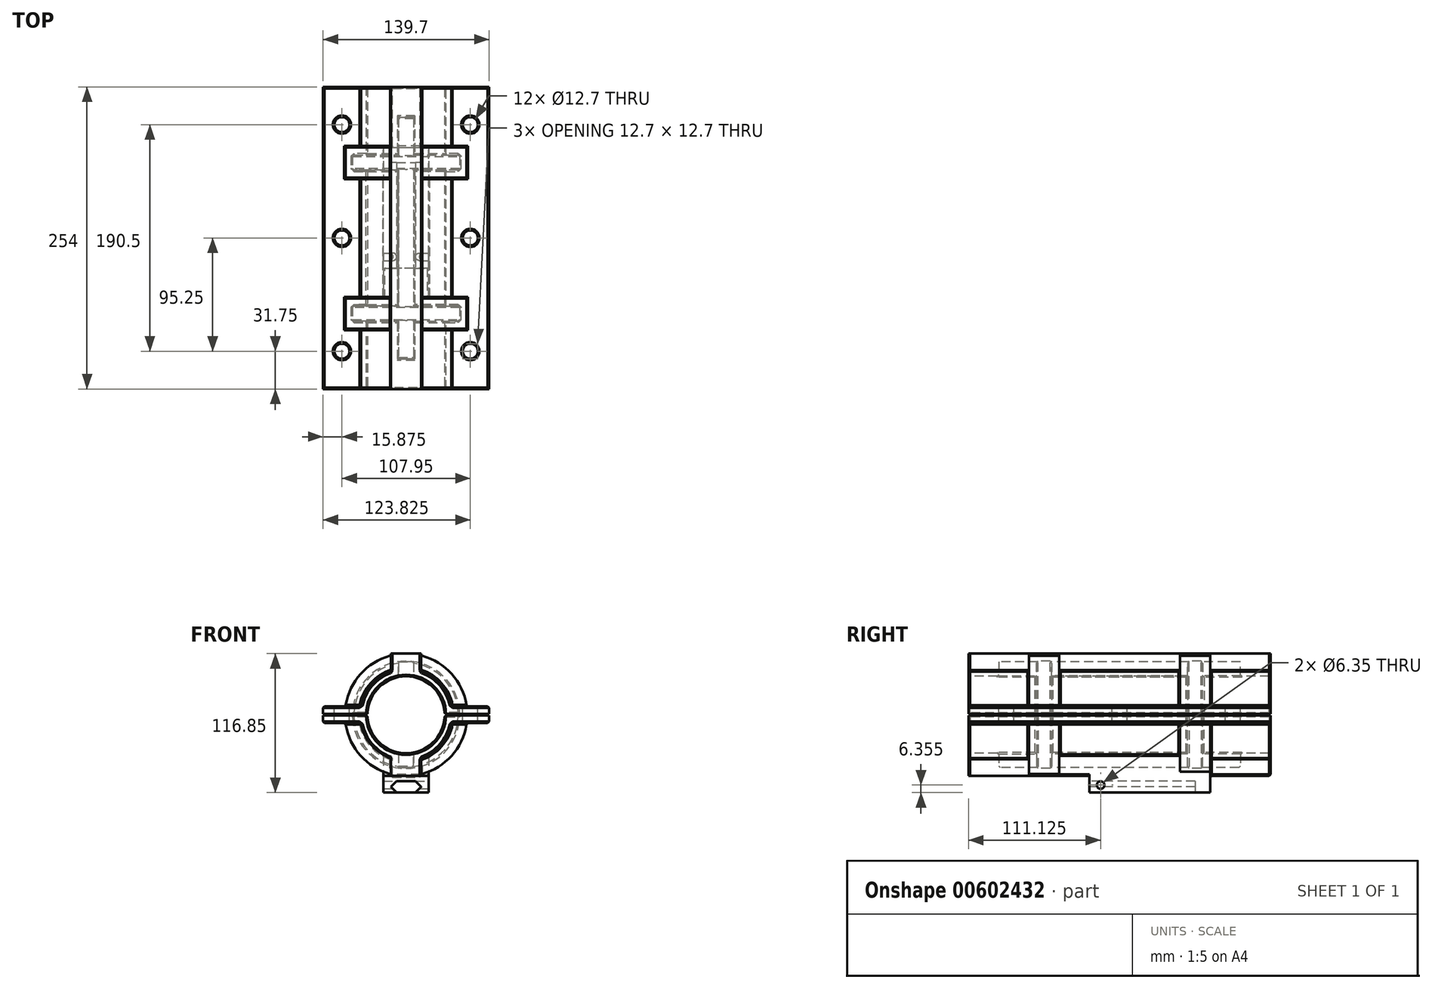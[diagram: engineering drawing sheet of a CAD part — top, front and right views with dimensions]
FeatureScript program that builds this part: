
annotation { "Feature Type Name" : "Feature", "Feature Type Description" : "" }
export const myFeature = defineFeature(function(context is Context, id is Id, definition is map)
    precondition{}
    {
        {
            var Q0;
            Q0=qCreatedBy(makeId("Front.planeOp"),FACE);
            var sketch = newSketch(context, id + "F0", { "sketchPlane" : qUnion([Q0])});
            skArc(sketch, "E0", {"start": v(-32.38, -0.64) * mm, "mid": v(0, -32.39) * mm, "end": v(32.38, -0.63) * mm});
            skLineSegment(sketch, "E1", {"start": v(0, 38.74) * mm, "end": v(0, -51.44) * mm, "construction": true});
            skLineSegment(sketch, "E2", {"start": v(-32.39, 0) * mm, "end": v(32.39, 0) * mm, "construction": true});
            skLineSegment(sketch, "E3", {"start": v(-32.38, 0.63) * mm, "end": v(-69.85, 0.63) * mm});
            skLineSegment(sketch, "E4", {"start": v(-69.85, 0.64) * mm, "end": v(-69.85, 6.98) * mm});
            skLineSegment(sketch, "E5", {"start": v(-69.85, 6.98) * mm, "end": v(-38.1, 6.98) * mm});
            skLineSegment(sketch, "E6.MirrorCS", {"start": v(32.38, 0.63) * mm, "end": v(69.85, 0.63) * mm});
            skLineSegment(sketch, "E7.MirrorCS", {"start": v(69.85, 0.64) * mm, "end": v(69.85, 6.98) * mm});
            skLineSegment(sketch, "E8.MirrorCS", {"start": v(69.85, 6.98) * mm, "end": v(38.1, 6.98) * mm});
            skLineSegment(sketch, "E9.MirrorCS", {"start": v(-32.38, -0.63) * mm, "end": v(-69.85, -0.63) * mm});
            skLineSegment(sketch, "E10.MirrorCS", {"start": v(-69.85, -6.98) * mm, "end": v(-38.1, -6.98) * mm});
            skLineSegment(sketch, "E11.MirrorCS", {"start": v(-69.85, -0.64) * mm, "end": v(-69.85, -6.98) * mm});
            skLineSegment(sketch, "E12.MirrorCS", {"start": v(69.85, -6.98) * mm, "end": v(38.1, -6.98) * mm});
            skLineSegment(sketch, "E13.MirrorCS", {"start": v(69.85, -0.64) * mm, "end": v(69.85, -6.98) * mm});
            skLineSegment(sketch, "E14.MirrorCS", {"start": v(32.38, -0.63) * mm, "end": v(69.85, -0.63) * mm});
            skArc(sketch, "E15.trimOffspring", {"start": v(-38.1, -6.98) * mm, "mid": v(-29.4, -25.22) * mm, "end": v(-12.7, -36.6) * mm});
            skArc(sketch, "E16.trimOffspring", {"start": v(38.1, 6.98) * mm, "mid": v(29.4, 25.22) * mm, "end": v(12.7, 36.6) * mm});
            skArc(sketch, "E17.trimOffspring", {"start": v(32.38, 0.63) * mm, "mid": v(0, 32.39) * mm, "end": v(-32.38, 0.64) * mm});
            skLineSegment(sketch, "E18", {"start": v(-12.7, 36.6) * mm, "end": v(-12.7, 51.44) * mm});
            skLineSegment(sketch, "E19", {"start": v(12.7, 51.44) * mm, "end": v(12.7, 36.6) * mm});
            skArc(sketch, "E20.trimOffspring", {"start": v(-12.7, 36.6) * mm, "mid": v(-29.4, 25.22) * mm, "end": v(-38.1, 6.98) * mm});
            skLineSegment(sketch, "E21", {"start": v(-12.7, 51.44) * mm, "end": v(12.7, 51.44) * mm});
            skLineSegment(sketch, "E22", {"start": v(-12.7, -36.6) * mm, "end": v(-12.7, -51.44) * mm});
            skLineSegment(sketch, "E23", {"start": v(-12.7, -51.44) * mm, "end": v(12.7, -51.44) * mm});
            skLineSegment(sketch, "E24", {"start": v(12.7, -51.44) * mm, "end": v(12.7, -36.6) * mm});
            skLineSegment(sketch, "E25", {"start": v(0, 38.74) * mm, "end": v(0, 51.44) * mm, "construction": true});
            skArc(sketch, "E26.trimOffspring", {"start": v(12.7, -36.6) * mm, "mid": v(29.4, -25.22) * mm, "end": v(38.1, -6.98) * mm});
            skCircle(sketch, "E27", {"center": v(0, 0) * mm, "radius": 38.74 * mm, "construction": true});
            skPoint(sketch, "E28", {"position": v(0, -38.74) * mm});
            skSolve(sketch);
        }
        {
            var Q0;
            Q0 = qSketchRegion(id + "F0", true);
            extrude(context, id + "F1", {"entities" : qUnion([Q0]), "oppositeDirection" : true, "depth" : 254 * mm, "offsetDistance" : 25.4 * mm});
        }
        {
            var Q0;
            Q0=qCreatedBy(makeId("Top.planeOp"),FACE);
            var sketch = newSketch(context, id + "F2", { "sketchPlane" : qUnion([Q0])});
            skLineSegment(sketch, "E29", {"start": v(0, 0) * mm, "end": v(0, 254) * mm, "construction": true});
            skLineSegment(sketch, "E30", {"start": v(0, 254) * mm, "end": v(32.39, 254) * mm, "construction": true});
            skLineSegment(sketch, "E31", {"start": v(32.38, 254) * mm, "end": v(32.39, 196.85) * mm});
            skLineSegment(sketch, "E32", {"start": v(32.39, 69.85) * mm, "end": v(45.09, 69.85) * mm});
            skLineSegment(sketch, "E33", {"start": v(45.09, 69.85) * mm, "end": v(45.09, 57.15) * mm});
            skLineSegment(sketch, "E34", {"start": v(45.09, 57.15) * mm, "end": v(32.39, 57.15) * mm});
            skLineSegment(sketch, "E35", {"start": v(32.39, 57.15) * mm, "end": v(32.39, 0) * mm});
            skLineSegment(sketch, "E36", {"start": v(32.39, 0) * mm, "end": v(38.74, 0) * mm});
            skLineSegment(sketch, "E37", {"start": v(38.74, 0) * mm, "end": v(38.74, 50.8) * mm});
            skLineSegment(sketch, "E38", {"start": v(38.74, 50.8) * mm, "end": v(51.44, 50.8) * mm});
            skLineSegment(sketch, "E39", {"start": v(51.44, 50.8) * mm, "end": v(51.44, 76.2) * mm});
            skLineSegment(sketch, "E40", {"start": v(51.44, 76.2) * mm, "end": v(38.74, 76.2) * mm});
            skLineSegment(sketch, "E41", {"start": v(38.74, 76.2) * mm, "end": v(38.74, 177.8) * mm});
            skLineSegment(sketch, "E42", {"start": v(38.74, 254) * mm, "end": v(32.39, 254) * mm});
            skLineSegment(sketch, "E43", {"start": v(69.85, 127) * mm, "end": v(-69.85, 127) * mm, "construction": true});
            skPoint(sketch, "E43.startSnap0", {"position": v(0, 127) * mm});
            skLineSegment(sketch, "E44.MirrorCS", {"start": v(51.44, 177.8) * mm, "end": v(38.74, 177.8) * mm});
            skLineSegment(sketch, "E45.MirrorCS", {"start": v(51.44, 203.2) * mm, "end": v(51.44, 177.8) * mm});
            skLineSegment(sketch, "E46.MirrorCS", {"start": v(38.74, 203.2) * mm, "end": v(51.44, 203.2) * mm});
            skLineSegment(sketch, "E47.MirrorCS", {"start": v(45.09, 196.85) * mm, "end": v(32.38, 196.85) * mm});
            skLineSegment(sketch, "E48.MirrorCS", {"start": v(32.39, 184.15) * mm, "end": v(45.09, 184.15) * mm});
            skLineSegment(sketch, "E49.MirrorCS", {"start": v(45.09, 184.15) * mm, "end": v(45.09, 196.85) * mm});
            skLineSegment(sketch, "E50.trimOffspring", {"start": v(38.73, 203.2) * mm, "end": v(38.73, 254) * mm});
            skLineSegment(sketch, "E51.trimOffspring", {"start": v(32.39, 184.15) * mm, "end": v(32.39, 69.85) * mm});
            skSolve(sketch);
        }
        {
            var Q0;
            Q0 = qSketchRegion(id + "F2", true);
            var Q1;
            Q1=sQuery(id+"F2.wireOp",EDGE,"E29");
            revolve(context, id + "F3", {"operationType" : NewBodyOperationType.ADD, "entities" : qUnion([Q0]), "axis" : qUnion([Q1]), "revolveType" : RevolveType.FULL});
        }
        {
            var Q0;
            Q0=qCreatedBy(makeId("Top.planeOp"),FACE);
            var sketch = newSketch(context, id + "F4", { "sketchPlane" : qUnion([Q0])});
            skLineSegment(sketch, "E52", {"start": v(0, 0) * mm, "end": v(0, 254) * mm, "construction": true});
            skLineSegment(sketch, "E53", {"start": v(0, 254) * mm, "end": v(32.39, 254) * mm, "construction": true});
            skLineSegment(sketch, "E54", {"start": v(32.39, 254) * mm, "end": v(32.39, 196.85) * mm, "construction": true});
            skLineSegment(sketch, "E55", {"start": v(32.39, 196.85) * mm, "end": v(45.08, 196.85) * mm});
            skLineSegment(sketch, "E56", {"start": v(45.08, 196.85) * mm, "end": v(45.08, 184.15) * mm});
            skLineSegment(sketch, "E57", {"start": v(45.08, 184.15) * mm, "end": v(32.39, 184.15) * mm});
            skLineSegment(sketch, "E58", {"start": v(32.39, 184.15) * mm, "end": v(32.39, 196.85) * mm});
            skLineSegment(sketch, "E59", {"start": v(0, 127) * mm, "end": v(69.85, 127) * mm, "construction": true});
            skPoint(sketch, "E59.endSnap0", {"position": v(0, 127) * mm});
            skLineSegment(sketch, "E60.MirrorCS", {"start": v(32.39, 69.85) * mm, "end": v(32.39, 57.15) * mm});
            skLineSegment(sketch, "E61.MirrorCS", {"start": v(32.39, 57.15) * mm, "end": v(45.09, 57.15) * mm});
            skLineSegment(sketch, "E62.MirrorCS", {"start": v(45.09, 57.15) * mm, "end": v(45.09, 69.85) * mm});
            skLineSegment(sketch, "E63.MirrorCS", {"start": v(45.09, 69.85) * mm, "end": v(32.39, 69.85) * mm});
            skSolve(sketch);
        }
        {
            var Q0;
            Q0 = qSketchRegion(id + "F4", true);
            var Q1;
            Q1=sQuery(id+"F4.wireOp",EDGE,"E52");
            revolve(context, id + "F5", {"operationType" : NewBodyOperationType.REMOVE, "entities" : qUnion([Q0]), "axis" : qUnion([Q1]), "revolveType" : RevolveType.FULL, "oppositeDirection" : true});
        }
        {
            var Q0;
            Q0=qCreatedBy(makeId("Front.planeOp"),FACE);
            var sketch = newSketch(context, id + "F6", { "sketchPlane" : qUnion([Q0])});
            skLineSegment(sketch, "E64", {"start": v(0, -32.39) * mm, "end": v(0, 32.39) * mm, "construction": true});
            skLineSegment(sketch, "E65", {"start": v(-69.85, 0) * mm, "end": v(69.85, 0) * mm, "construction": true});
            skLineSegment(sketch, "E66", {"start": v(-69.85, 0) * mm, "end": v(-69.85, 0.64) * mm});
            skLineSegment(sketch, "E67", {"start": v(-69.85, 0.64) * mm, "end": v(69.85, 0.64) * mm});
            skLineSegment(sketch, "E68", {"start": v(69.85, 0.64) * mm, "end": v(69.85, 0) * mm});
            skLineSegment(sketch, "E69.MirrorCS", {"start": v(-69.85, 0) * mm, "end": v(-69.85, -0.64) * mm});
            skLineSegment(sketch, "E70.MirrorCS", {"start": v(-69.85, -0.64) * mm, "end": v(69.85, -0.64) * mm});
            skLineSegment(sketch, "E71.MirrorCS", {"start": v(69.85, -0.64) * mm, "end": v(69.85, 0) * mm});
            skSolve(sketch);
        }
        {
            var Q0;
            Q0 = qSketchRegion(id + "F6", true);
            extrude(context, id + "F7", {"entities" : qUnion([Q0]), "operationType" : NewBodyOperationType.REMOVE, "oppositeDirection" : true, "depth" : 254 * mm, "offsetDistance" : 25.4 * mm});
        }
        {
            var Q0;
            Q0=makeQuery(id+"F1.opExtrude","SWEPT_FACE",FACE,{"disambiguationData":[OSD([sQuery(id+"F0.wireOp",EDGE,"E23")])]});
            cPlane(context, id + "F8", {"entities" : qUnion([Q0]), "cplaneType" : CPlaneType.OFFSET, "offset" : 13.97 * mm, "width" : 152.4 * mm, "height" : 152.4 * mm});
        }
        {
            var Q0;
            Q0=qCreatedBy(id+"F8.planeOp",FACE);
            var sketch = newSketch(context, id + "F9", { "sketchPlane" : qUnion([Q0])});
            skLineSegment(sketch, "E72", {"start": v(0, 0) * mm, "end": v(0, -254) * mm, "construction": true});
            skLineSegment(sketch, "E73.bottom", {"start": v(-19.05, -101.6) * mm, "end": v(19.05, -101.6) * mm});
            skLineSegment(sketch, "E73.top", {"start": v(-19.05, -203.2) * mm, "end": v(19.05, -203.2) * mm});
            skLineSegment(sketch, "E73.left", {"start": v(-19.05, -101.6) * mm, "end": v(-19.05, -203.2) * mm});
            skLineSegment(sketch, "E73.right", {"start": v(19.05, -101.6) * mm, "end": v(19.05, -203.2) * mm});
            skPoint(sketch, "E73.middle", {"position": v(0, -152.4) * mm});
            skSolve(sketch);
        }
        {
            var Q0;
            Q0 = qSketchRegion(id + "F9", true);
            extrude(context, id + "F10", {"entities" : qUnion([Q0]), "operationType" : NewBodyOperationType.ADD, "endBound" : BoundingType.UP_TO_NEXT, "oppositeDirection" : true, "depth" : 25.4 * mm, "offsetDistance" : 25.4 * mm});
        }
        {
            var Q0;
            Q0=makeQuery(id+"F10.opExtrude","SWEPT_FACE",FACE,{"disambiguationData":[OSD([sQuery(id+"F9.wireOp",EDGE,"E73.bottom")])]});
            var sketch = newSketch(context, id + "F11", { "sketchPlane" : qUnion([Q0])});
            skLineSegment(sketch, "E74", {"start": v(0, -65.4) * mm, "end": v(-7.94, -65.4) * mm});
            skLineSegment(sketch, "E75", {"start": v(-12.7, -60.64) * mm, "end": v(-7.94, -65.4) * mm});
            skLineSegment(sketch, "E76", {"start": v(-7.94, -55.88) * mm, "end": v(-12.7, -60.64) * mm});
            skLineSegment(sketch, "E77", {"start": v(-7.94, -55.88) * mm, "end": v(0, -55.88) * mm});
            skLineSegment(sketch, "E78", {"start": v(0, -51.44) * mm, "end": v(0, -65.4) * mm, "construction": true});
            skLineSegment(sketch, "E79.MirrorCS", {"start": v(0, -65.4) * mm, "end": v(7.94, -65.4) * mm});
            skLineSegment(sketch, "E80.MirrorCS", {"start": v(12.7, -60.64) * mm, "end": v(7.94, -65.4) * mm});
            skLineSegment(sketch, "E81.MirrorCS", {"start": v(7.94, -55.88) * mm, "end": v(12.7, -60.64) * mm});
            skLineSegment(sketch, "E82.MirrorCS", {"start": v(7.94, -55.88) * mm, "end": v(0, -55.88) * mm});
            skSolve(sketch);
        }
        {
            var Q0;
            Q0 = qSketchRegion(id + "F11", true);
            extrude(context, id + "F12", {"entities" : qUnion([Q0]), "operationType" : NewBodyOperationType.REMOVE, "oppositeDirection" : true, "depth" : 88.9 * mm, "offsetDistance" : 25.4 * mm});
        }
        {
            var Q0;
            {var subQ2=sQuery(id+"F9.wireOp",EDGE,"E73.right");Q0=makeQuery(id+"F10.boolean.opBoolean","SPLIT",FACE,{"disambiguationData":[TD([makeQuery(id+"F1.opExtrude","SWEPT_FACE",FACE,{"disambiguationData":[OSD([sQuery(id+"F0.wireOp",EDGE,"E26.trimOffspring")])]})])],"derivedFrom":makeQuery(id+"F10.opExtrude","SWEPT_FACE",FACE,{"disambiguationData":[OSD([subQ2])]})});}
            var sketch = newSketch(context, id + "F13", { "sketchPlane" : qUnion([Q0])});
            skCircle(sketch, "E83", {"center": v(111.12, -59.06) * mm, "radius": 3.18 * mm});
            skSolve(sketch);
        }
        {
            var Q0;
            Q0 = qSketchRegion(id + "F13", true);
            extrude(context, id + "F14", {"entities" : qUnion([Q0]), "operationType" : NewBodyOperationType.REMOVE, "endBound" : BoundingType.THROUGH_ALL, "oppositeDirection" : true, "depth" : 25.4 * mm, "offsetDistance" : 25.4 * mm});
        }
        {
            var Q0;
            {var subQ0=sQuery(id+"F0.wireOp",EDGE,"E17.trimOffspring");var subQ1=sQuery(id+"F0.wireOp",EDGE,"E15.trimOffspring");var subQ2=sQuery(id+"F0.wireOp",EDGE,"E14.MirrorCS");var subQ3=sQuery(id+"F0.wireOp",EDGE,"E13.MirrorCS");var subQ4=sQuery(id+"F0.wireOp",EDGE,"E12.MirrorCS");var subQ5=sQuery(id+"F0.wireOp",EDGE,"E0");var subQ6=sQuery(id+"F0.wireOp",EDGE,"E9.MirrorCS");var subQ7=sQuery(id+"F0.wireOp",EDGE,"E10.MirrorCS");var subQ8=sQuery(id+"F0.wireOp",EDGE,"E22");var subQ9=sQuery(id+"F0.wireOp",EDGE,"E11.MirrorCS");var subQ10=sQuery(id+"F0.wireOp",EDGE,"E23");var subQ11=sQuery(id+"F0.wireOp",EDGE,"E24");var subQ12=sQuery(id+"F0.wireOp",EDGE,"E26.trimOffspring");Q0=makeQuery(id+"F7.boolean.opBoolean","SPLIT",FACE,{"disambiguationData":[TD([makeQuery(id+"F1.opExtrude","SWEPT_FACE",FACE,{"disambiguationData":[OSD([subQ6])]})])],"derivedFrom":makeQuery(id+"F3.boolean.opBoolean","MERGE",FACE,{"derivedFrom":[makeQuery(id+"F1.opExtrude","CAP_FACE",FACE,{"disambiguationData":[OSD([subQ5,subQ6,subQ7,subQ9,subQ4,subQ3,subQ2,subQ1,subQ8,subQ10,subQ11,subQ12])],"isStart":true}),makeQuery(id+"F1.opExtrude","CAP_FACE",FACE,{"disambiguationData":[OSD([sQuery(id+"F0.wireOp",EDGE,"E3"),sQuery(id+"F0.wireOp",EDGE,"E4"),sQuery(id+"F0.wireOp",EDGE,"E5"),sQuery(id+"F0.wireOp",EDGE,"E6.MirrorCS"),sQuery(id+"F0.wireOp",EDGE,"E7.MirrorCS"),sQuery(id+"F0.wireOp",EDGE,"E8.MirrorCS"),sQuery(id+"F0.wireOp",EDGE,"E16.trimOffspring"),subQ0,sQuery(id+"F0.wireOp",EDGE,"E18"),sQuery(id+"F0.wireOp",EDGE,"E19"),sQuery(id+"F0.wireOp",EDGE,"E20.trimOffspring"),sQuery(id+"F0.wireOp",EDGE,"E21")])],"isStart":true}),makeQuery(id+"F3.opRevolve","SWEPT_FACE",FACE,{"disambiguationData":[OSD([sQuery(id+"F2.wireOp",EDGE,"E36")])]})]})});}
            cPlane(context, id + "F15", {"entities" : qUnion([Q0]), "cplaneType" : CPlaneType.OFFSET, "offset" : 25.4 * mm, "oppositeDirection" : true, "width" : 152.4 * mm, "height" : 152.4 * mm});
        }
        {
            var Q0;
            Q0=qCreatedBy(id+"F15.planeOp",FACE);
            var sketch = newSketch(context, id + "F16", { "sketchPlane" : qUnion([Q0])});
            skLineSegment(sketch, "E84", {"start": v(0, 51.44) * mm, "end": v(0, -51.44) * mm, "construction": true});
            skLineSegment(sketch, "E85", {"start": v(-6.35, 44.46) * mm, "end": v(6.35, 44.46) * mm});
            skLineSegment(sketch, "E86", {"start": v(6.35, 44.46) * mm, "end": v(6.35, 31.76) * mm});
            skLineSegment(sketch, "E87", {"start": v(6.35, 31.76) * mm, "end": v(-6.35, 31.76) * mm});
            skLineSegment(sketch, "E88", {"start": v(-6.35, 31.76) * mm, "end": v(-6.35, 44.46) * mm});
            skLineSegment(sketch, "E89", {"start": v(-62.32, 0) * mm, "end": v(62.17, 0) * mm, "construction": true});
            skLineSegment(sketch, "E90.MirrorCS", {"start": v(6.35, -31.76) * mm, "end": v(-6.35, -31.76) * mm});
            skLineSegment(sketch, "E91.MirrorCS", {"start": v(6.35, -44.46) * mm, "end": v(6.35, -31.76) * mm});
            skLineSegment(sketch, "E92.MirrorCS", {"start": v(-6.35, -44.46) * mm, "end": v(6.35, -44.46) * mm});
            skLineSegment(sketch, "E93.MirrorCS", {"start": v(-6.35, -31.76) * mm, "end": v(-6.35, -44.46) * mm});
            skSolve(sketch);
        }
        {
            var Q0;
            Q0 = qSketchRegion(id + "F16", true);
            extrude(context, id + "F17", {"entities" : qUnion([Q0]), "operationType" : NewBodyOperationType.REMOVE, "oppositeDirection" : true, "depth" : 203.2 * mm, "offsetDistance" : 25.4 * mm});
        }
        {
            var Q0;
            {var subQ2=sQuery(id+"F0.wireOp",EDGE,"E23");Q0=makeQuery(id+"F10.boolean.opBoolean","SPLIT",FACE,{"disambiguationData":[TD([makeQuery(id+"F3.opRevolve","SWEPT_FACE",FACE,{"disambiguationData":[OSD([sQuery(id+"F2.wireOp",EDGE,"E36")])]})])],"derivedFrom":makeQuery(id+"F1.opExtrude","SWEPT_FACE",FACE,{"disambiguationData":[OSD([subQ2])]})});}
            var sketch = newSketch(context, id + "F18", { "sketchPlane" : qUnion([Q0])});
            skLineSegment(sketch, "E94.bottom", {"start": v(-12.7, -101.6) * mm, "end": v(-19.05, -101.6) * mm});
            skLineSegment(sketch, "E94.top", {"start": v(-12.7, -76.2) * mm, "end": v(-19.05, -76.2) * mm});
            skLineSegment(sketch, "E94.left", {"start": v(-12.7, -101.6) * mm, "end": v(-12.7, -76.2) * mm});
            skLineSegment(sketch, "E94.right", {"start": v(-19.05, -101.6) * mm, "end": v(-19.05, -76.2) * mm});
            skLineSegment(sketch, "E95", {"start": v(0, 0) * mm, "end": v(0, -101.6) * mm, "construction": true});
            skLineSegment(sketch, "E96.MirrorCS", {"start": v(12.7, -101.6) * mm, "end": v(12.7, -76.2) * mm});
            skLineSegment(sketch, "E97.MirrorCS", {"start": v(12.7, -76.2) * mm, "end": v(19.05, -76.2) * mm});
            skLineSegment(sketch, "E98.MirrorCS", {"start": v(19.05, -101.6) * mm, "end": v(19.05, -76.2) * mm});
            skLineSegment(sketch, "E99.MirrorCS", {"start": v(12.7, -101.6) * mm, "end": v(19.05, -101.6) * mm});
            skSolve(sketch);
        }
        {
            var Q0;
            Q0 = qSketchRegion(id + "F18", true);
            extrude(context, id + "F19", {"entities" : qUnion([Q0]), "operationType" : NewBodyOperationType.ADD, "endBound" : BoundingType.UP_TO_NEXT, "oppositeDirection" : true, "depth" : 25.4 * mm, "offsetDistance" : 25.4 * mm});
        }
        {
            var Q0;
            {var subQ1=sQuery(id+"F0.wireOp",EDGE,"E4");var subQ22=sQuery(id+"F0.wireOp",EDGE,"E5");Q0=makeQuery(id+"F3.boolean.opBoolean","SPLIT",FACE,{"disambiguationData":[TD([makeQuery(id+"F1.opExtrude","SWEPT_FACE",FACE,{"disambiguationData":[OSD([subQ1])]})])],"derivedFrom":makeQuery(id+"F1.opExtrude","SWEPT_FACE",FACE,{"disambiguationData":[OSD([subQ22])]})});}
            var sketch = newSketch(context, id + "F20", { "sketchPlane" : qUnion([Q0])});
            skCircle(sketch, "E100", {"center": v(-53.98, 222.25) * mm, "radius": 6.35 * mm});
            skLineSegment(sketch, "E101", {"start": v(-53.98, 222.25) * mm, "end": v(-53.98, 127) * mm, "construction": true});
            skPoint(sketch, "E101.endSnap0", {"position": v(-69.85, 127) * mm});
            skCircle(sketch, "E102", {"center": v(-53.98, 127) * mm, "radius": 6.35 * mm});
            skLineSegment(sketch, "E103", {"start": v(-53.98, 127) * mm, "end": v(-69.85, 127) * mm, "construction": true});
            skCircle(sketch, "E104.MirrorC", {"center": v(-53.98, 31.75) * mm, "radius": 6.35 * mm});
            skLineSegment(sketch, "E105", {"start": v(0, 0) * mm, "end": v(0, 254) * mm, "construction": true});
            skCircle(sketch, "E106.MirrorC", {"center": v(53.97, 222.25) * mm, "radius": 6.35 * mm});
            skCircle(sketch, "E107.MirrorC", {"center": v(53.98, 127) * mm, "radius": 6.35 * mm});
            skCircle(sketch, "E108.MirrorC", {"center": v(53.98, 31.75) * mm, "radius": 6.35 * mm});
            skSolve(sketch);
        }
        {
            var Q0;
            Q0 = qSketchRegion(id + "F20", true);
            extrude(context, id + "F21", {"entities" : qUnion([Q0]), "operationType" : NewBodyOperationType.REMOVE, "endBound" : BoundingType.THROUGH_ALL, "oppositeDirection" : true, "depth" : 25.4 * mm, "offsetDistance" : 25.4 * mm});
        }
        {
            var Q0;
            Q0=makeQuery(id+"F3.boolean.opBoolean","INTERSECT",EDGE,{"derivedFrom":[makeQuery(id+"F1.opExtrude","SWEPT_FACE",FACE,{"disambiguationData":[OSD([sQuery(id+"F0.wireOp",EDGE,"E19")])]}),makeQuery(id+"F3.opRevolve","SWEPT_FACE",FACE,{"disambiguationData":[OSD([sQuery(id+"F2.wireOp",EDGE,"E45.MirrorCS")])]})]});
            var Q1;
            {var subQ0=sQuery(id+"F0.wireOp",EDGE,"E16.trimOffspring");var subQ1=sQuery(id+"F0.wireOp",EDGE,"E19");Q1=makeQuery(id+"F3.boolean.opBoolean","SPLIT",EDGE,{"disambiguationData":[TD([makeQuery(id+"F3.opRevolve","SWEPT_FACE",FACE,{"disambiguationData":[OSD([sQuery(id+"F2.wireOp",EDGE,"E36")])]})])],"derivedFrom":makeQuery(id+"F1.opExtrude","SWEPT_EDGE",EDGE,{"disambiguationData":[OSD([subQ0,subQ1])]})});}
            var Q2;
            {var subQ0=sQuery(id+"F2.wireOp",EDGE,"E38");Q2=makeQuery(id+"F3.boolean.opBoolean","SPLIT",EDGE,{"disambiguationData":[topologyDisambiguationEdgeConnected([makeQuery(id+"F1.opExtrude","SWEPT_FACE",FACE,{"disambiguationData":[OSD([sQuery(id+"F0.wireOp",EDGE,"E16.trimOffspring")])]}),makeQuery(id+"F3.opRevolve","SWEPT_FACE",FACE,{"disambiguationData":[OSD([subQ0])]})])],"derivedFrom":makeQuery(id+"F3.opRevolve","SWEPT_EDGE",EDGE,{"disambiguationData":[OSD([sQuery(id+"F2.wireOp",EDGE,"E37"),subQ0])]})});}
            var Q3;
            {var subQ1=sQuery(id+"F0.wireOp",EDGE,"E7.MirrorCS");var subQ19=sQuery(id+"F0.wireOp",EDGE,"E8.MirrorCS");Q3=makeQuery(id+"F3.boolean.opBoolean","SPLIT",FACE,{"disambiguationData":[TD([makeQuery(id+"F1.opExtrude","SWEPT_FACE",FACE,{"disambiguationData":[OSD([subQ1])]})])],"derivedFrom":makeQuery(id+"F1.opExtrude","SWEPT_FACE",FACE,{"disambiguationData":[OSD([subQ19])]})});}
            var Q4;
            Q4=makeQuery(id+"F3.boolean.opBoolean","INTERSECT",EDGE,{"derivedFrom":[makeQuery(id+"F1.opExtrude","SWEPT_FACE",FACE,{"disambiguationData":[OSD([sQuery(id+"F0.wireOp",EDGE,"E19")])]}),makeQuery(id+"F3.opRevolve","SWEPT_FACE",FACE,{"disambiguationData":[OSD([sQuery(id+"F2.wireOp",EDGE,"E39")])]})]});
            var Q5;
            Q5=makeQuery(id+"F3.boolean.opBoolean","SPLIT",FACE,{"disambiguationData":[TD([makeQuery(id+"F3.opRevolve","SWEPT_FACE",FACE,{"disambiguationData":[OSD([sQuery(id+"F2.wireOp",EDGE,"E40")])]})])],"derivedFrom":makeQuery(id+"F1.opExtrude","SWEPT_FACE",FACE,{"disambiguationData":[OSD([sQuery(id+"F0.wireOp",EDGE,"E16.trimOffspring")])]})});
            var Q6;
            {var subQ2=sQuery(id+"F0.wireOp",EDGE,"E16.trimOffspring");Q6=makeQuery(id+"F3.boolean.opBoolean","SPLIT",FACE,{"disambiguationData":[TD([makeQuery(id+"F3.opRevolve","SWEPT_FACE",FACE,{"disambiguationData":[OSD([sQuery(id+"F2.wireOp",EDGE,"E42")])]})])],"derivedFrom":makeQuery(id+"F1.opExtrude","SWEPT_FACE",FACE,{"disambiguationData":[OSD([subQ2])]})});}
            var Q7;
            Q7=makeQuery(id+"F3.boolean.opBoolean","SPLIT",FACE,{"disambiguationData":[TD([makeQuery(id+"F3.opRevolve","SWEPT_FACE",FACE,{"disambiguationData":[OSD([sQuery(id+"F2.wireOp",EDGE,"E40")])]})])],"derivedFrom":makeQuery(id+"F1.opExtrude","SWEPT_FACE",FACE,{"disambiguationData":[OSD([sQuery(id+"F0.wireOp",EDGE,"E20.trimOffspring")])]})});
            var Q8;
            {var subQ1=sQuery(id+"F0.wireOp",EDGE,"E4");var subQ22=sQuery(id+"F0.wireOp",EDGE,"E5");Q8=makeQuery(id+"F3.boolean.opBoolean","SPLIT",FACE,{"disambiguationData":[TD([makeQuery(id+"F1.opExtrude","SWEPT_FACE",FACE,{"disambiguationData":[OSD([subQ1])]})])],"derivedFrom":makeQuery(id+"F1.opExtrude","SWEPT_FACE",FACE,{"disambiguationData":[OSD([subQ22])]})});}
            var Q9;
            {var subQ2=sQuery(id+"F0.wireOp",EDGE,"E20.trimOffspring");Q9=makeQuery(id+"F3.boolean.opBoolean","SPLIT",FACE,{"disambiguationData":[TD([makeQuery(id+"F3.opRevolve","SWEPT_FACE",FACE,{"disambiguationData":[OSD([sQuery(id+"F2.wireOp",EDGE,"E36")])]})])],"derivedFrom":makeQuery(id+"F1.opExtrude","SWEPT_FACE",FACE,{"disambiguationData":[OSD([subQ2])]})});}
            var Q10;
            {var subQ1=sQuery(id+"F0.wireOp",EDGE,"E20.trimOffspring");Q10=makeQuery(id+"F3.boolean.opBoolean","SPLIT",FACE,{"disambiguationData":[TD([makeQuery(id+"F3.opRevolve","SWEPT_FACE",FACE,{"disambiguationData":[OSD([sQuery(id+"F2.wireOp",EDGE,"E42")])]})])],"derivedFrom":makeQuery(id+"F1.opExtrude","SWEPT_FACE",FACE,{"disambiguationData":[OSD([subQ1])]})});}
            var Q11;
            {var subQ8=sQuery(id+"F0.wireOp",EDGE,"E11.MirrorCS");var subQ9=sQuery(id+"F0.wireOp",EDGE,"E10.MirrorCS");Q11=makeQuery(id+"F3.boolean.opBoolean","SPLIT",FACE,{"disambiguationData":[TD([makeQuery(id+"F1.opExtrude","SWEPT_FACE",FACE,{"disambiguationData":[OSD([subQ8])]})])],"derivedFrom":makeQuery(id+"F1.opExtrude","SWEPT_FACE",FACE,{"disambiguationData":[OSD([subQ9])]})});}
            var Q12;
            Q12=makeQuery(id+"F3.boolean.opBoolean","SPLIT",FACE,{"disambiguationData":[TD([makeQuery(id+"F3.opRevolve","SWEPT_FACE",FACE,{"disambiguationData":[OSD([sQuery(id+"F2.wireOp",EDGE,"E40")])]})])],"derivedFrom":makeQuery(id+"F1.opExtrude","SWEPT_FACE",FACE,{"disambiguationData":[OSD([sQuery(id+"F0.wireOp",EDGE,"E15.trimOffspring")])]})});
            var Q13;
            {var subQ1=sQuery(id+"F0.wireOp",EDGE,"E15.trimOffspring");Q13=makeQuery(id+"F3.boolean.opBoolean","SPLIT",FACE,{"disambiguationData":[TD([makeQuery(id+"F3.opRevolve","SWEPT_FACE",FACE,{"disambiguationData":[OSD([sQuery(id+"F2.wireOp",EDGE,"E42")])]})])],"derivedFrom":makeQuery(id+"F1.opExtrude","SWEPT_FACE",FACE,{"disambiguationData":[OSD([subQ1])]})});}
            var Q14;
            {var subQ2=sQuery(id+"F0.wireOp",EDGE,"E26.trimOffspring");Q14=makeQuery(id+"F3.boolean.opBoolean","SPLIT",FACE,{"disambiguationData":[TD([makeQuery(id+"F3.opRevolve","SWEPT_FACE",FACE,{"disambiguationData":[OSD([sQuery(id+"F2.wireOp",EDGE,"E42")])]})])],"derivedFrom":makeQuery(id+"F1.opExtrude","SWEPT_FACE",FACE,{"disambiguationData":[OSD([subQ2])]})});}
            var Q15;
            Q15=makeQuery(id+"F3.boolean.opBoolean","SPLIT",FACE,{"disambiguationData":[TD([makeQuery(id+"F3.opRevolve","SWEPT_FACE",FACE,{"disambiguationData":[OSD([sQuery(id+"F2.wireOp",EDGE,"E40")])]})])],"derivedFrom":makeQuery(id+"F1.opExtrude","SWEPT_FACE",FACE,{"disambiguationData":[OSD([sQuery(id+"F0.wireOp",EDGE,"E26.trimOffspring")])]})});
            var Q16;
            {var subQ2=sQuery(id+"F0.wireOp",EDGE,"E26.trimOffspring");Q16=makeQuery(id+"F3.boolean.opBoolean","SPLIT",FACE,{"disambiguationData":[TD([makeQuery(id+"F3.opRevolve","SWEPT_FACE",FACE,{"disambiguationData":[OSD([sQuery(id+"F2.wireOp",EDGE,"E36")])]})])],"derivedFrom":makeQuery(id+"F1.opExtrude","SWEPT_FACE",FACE,{"disambiguationData":[OSD([subQ2])]})});}
            var Q17;
            {var subQ6=sQuery(id+"F0.wireOp",EDGE,"E13.MirrorCS");var subQ7=sQuery(id+"F0.wireOp",EDGE,"E12.MirrorCS");Q17=makeQuery(id+"F3.boolean.opBoolean","SPLIT",FACE,{"disambiguationData":[TD([makeQuery(id+"F1.opExtrude","SWEPT_FACE",FACE,{"disambiguationData":[OSD([subQ6])]})])],"derivedFrom":makeQuery(id+"F1.opExtrude","SWEPT_FACE",FACE,{"disambiguationData":[OSD([subQ7])]})});}
            var Q18;
            Q18=makeQuery(id+"F3.boolean.opBoolean","INTERSECT",EDGE,{"derivedFrom":[makeQuery(id+"F1.opExtrude","SWEPT_FACE",FACE,{"disambiguationData":[OSD([sQuery(id+"F0.wireOp",EDGE,"E24")])]}),makeQuery(id+"F3.opRevolve","SWEPT_FACE",FACE,{"disambiguationData":[OSD([sQuery(id+"F2.wireOp",EDGE,"E39")])]})]});
            var Q19;
            Q19=makeQuery(id+"F10.opExtrude","TWEAK_EDGE",EDGE,{"derivedFrom":[makeQuery(id+"F3.boolean.opBoolean","SPLIT",FACE,{"disambiguationData":[TD([makeQuery(id+"F1.opExtrude","SWEPT_FACE",FACE,{"disambiguationData":[OSD([sQuery(id+"F0.wireOp",EDGE,"E12.MirrorCS")])]})])],"derivedFrom":makeQuery(id+"F3.opRevolve","SWEPT_FACE",FACE,{"disambiguationData":[OSD([sQuery(id+"F2.wireOp",EDGE,"E45.MirrorCS")])]})}),makeQuery(id+"F9.imprint","IMPRINT",EDGE,{"derivedFrom":sQuery(id+"F9.wireOp",EDGE,"E73.right")})]});
            var Q20;
            Q20=makeQuery(id+"F10.opExtrude","TWEAK_EDGE",EDGE,{"derivedFrom":[makeQuery(id+"F3.boolean.opBoolean","SPLIT",FACE,{"disambiguationData":[TD([makeQuery(id+"F1.opExtrude","SWEPT_FACE",FACE,{"disambiguationData":[OSD([sQuery(id+"F0.wireOp",EDGE,"E10.MirrorCS")])]})])],"derivedFrom":makeQuery(id+"F3.opRevolve","SWEPT_FACE",FACE,{"disambiguationData":[OSD([sQuery(id+"F2.wireOp",EDGE,"E45.MirrorCS")])]})}),makeQuery(id+"F9.imprint","IMPRINT",EDGE,{"derivedFrom":sQuery(id+"F9.wireOp",EDGE,"E73.left")})]});
            var Q21;
            Q21=makeQuery(id+"F3.boolean.opBoolean","INTERSECT",EDGE,{"derivedFrom":[makeQuery(id+"F1.opExtrude","SWEPT_FACE",FACE,{"disambiguationData":[OSD([sQuery(id+"F0.wireOp",EDGE,"E22")])]}),makeQuery(id+"F3.opRevolve","SWEPT_FACE",FACE,{"disambiguationData":[OSD([sQuery(id+"F2.wireOp",EDGE,"E39")])]})]});
            var Q22;
            Q22=makeQuery(id+"F19.boolean.opBoolean","MERGE",EDGE,{"derivedFrom":[makeQuery(id+"F10.opExtrude","TWEAK_EDGE",EDGE,{"derivedFrom":[makeQuery(id+"F1.opExtrude","SWEPT_FACE",FACE,{"disambiguationData":[OSD([sQuery(id+"F0.wireOp",EDGE,"E23")])]}),makeQuery(id+"F9.imprint","IMPRINT",EDGE,{"derivedFrom":sQuery(id+"F9.wireOp",EDGE,"E73.bottom")})]}),makeQuery(id+"F19.opExtrude","CAP_EDGE",EDGE,{"disambiguationData":[OSD([sQuery(id+"F18.wireOp",EDGE,"E94.bottom")])],"isStart":true}),makeQuery(id+"F19.opExtrude","CAP_EDGE",EDGE,{"disambiguationData":[OSD([sQuery(id+"F18.wireOp",EDGE,"E99.MirrorCS")])],"isStart":true})]});
            var Q23;
            Q23=makeQuery(id+"F19.opExtrude","CAP_EDGE",EDGE,{"disambiguationData":[OSD([sQuery(id+"F18.wireOp",EDGE,"E98.MirrorCS")])],"isStart":true});
            var Q24;
            Q24=makeQuery(id+"F19.opExtrude","CAP_EDGE",EDGE,{"disambiguationData":[OSD([sQuery(id+"F18.wireOp",EDGE,"E94.right")])],"isStart":true});
            var Q25;
            {var subQ2=sQuery(id+"F0.wireOp",EDGE,"E23");Q25=makeQuery(id+"F10.boolean.opBoolean","SPLIT",FACE,{"disambiguationData":[TD([makeQuery(id+"F3.opRevolve","SWEPT_FACE",FACE,{"disambiguationData":[OSD([sQuery(id+"F2.wireOp",EDGE,"E42")])]})])],"derivedFrom":makeQuery(id+"F1.opExtrude","SWEPT_FACE",FACE,{"disambiguationData":[OSD([subQ2])]})});}
            var Q26;
            Q26=makeQuery(id+"F3.boolean.opBoolean","INTERSECT",EDGE,{"derivedFrom":[makeQuery(id+"F1.opExtrude","SWEPT_FACE",FACE,{"disambiguationData":[OSD([sQuery(id+"F0.wireOp",EDGE,"E18")])]}),makeQuery(id+"F3.opRevolve","SWEPT_FACE",FACE,{"disambiguationData":[OSD([sQuery(id+"F2.wireOp",EDGE,"E45.MirrorCS")])]})]});
            var Q27;
            Q27=makeQuery(id+"F3.boolean.opBoolean","INTERSECT",EDGE,{"derivedFrom":[makeQuery(id+"F1.opExtrude","SWEPT_FACE",FACE,{"disambiguationData":[OSD([sQuery(id+"F0.wireOp",EDGE,"E18")])]}),makeQuery(id+"F3.opRevolve","SWEPT_FACE",FACE,{"disambiguationData":[OSD([sQuery(id+"F2.wireOp",EDGE,"E39")])]})]});
            chamfer(context, id + "F22", {"entities" : qUnion([Q0, Q1, Q2, Q3, Q4, Q5, Q6, Q7, Q8, Q9, Q10, Q11, Q12, Q13, Q14, Q15, Q16, Q17, Q18, Q19, Q20, Q21, Q22, Q23, Q24, Q25, Q26, Q27]), "width" : 1.27 * mm, "tangentPropagation" : true});
        }
        {
            var Q0;
            {var subQ2=makeQuery(id+"F3.opRevolve","SWEPT_FACE",FACE,{"disambiguationData":[OSD([sQuery(id+"F2.wireOp",EDGE,"E32")])]});var subQ4=makeQuery(id+"F1.opExtrude","SWEPT_FACE",FACE,{"disambiguationData":[OSD([sQuery(id+"F0.wireOp",EDGE,"E9.MirrorCS")])]});Q0=makeQuery(id+"F17.boolean.opBoolean","SPLIT",FACE,{"disambiguationData":[TD([subQ4])],"derivedFrom":makeQuery(id+"F7.boolean.opBoolean","SPLIT",FACE,{"disambiguationData":[TD([subQ4])],"derivedFrom":makeQuery(id+"F5.boolean.opBoolean","SPLIT",FACE,{"disambiguationData":[TD([subQ2])],"derivedFrom":makeQuery(id+"F3.boolean.opBoolean","MERGE",FACE,{"derivedFrom":[makeQuery(id+"F1.opExtrude","SWEPT_FACE",FACE,{"disambiguationData":[OSD([sQuery(id+"F0.wireOp",EDGE,"E0")])]}),makeQuery(id+"F1.opExtrude","SWEPT_FACE",FACE,{"disambiguationData":[OSD([sQuery(id+"F0.wireOp",EDGE,"E17.trimOffspring")])]}),makeQuery(id+"F3.opRevolve","SWEPT_FACE",FACE,{"disambiguationData":[OSD([sQuery(id+"F2.wireOp",EDGE,"E31")])]}),makeQuery(id+"F3.opRevolve","SWEPT_FACE",FACE,{"disambiguationData":[OSD([sQuery(id+"F2.wireOp",EDGE,"E35")])]}),makeQuery(id+"F3.opRevolve","SWEPT_FACE",FACE,{"disambiguationData":[OSD([sQuery(id+"F2.wireOp",EDGE,"E51.trimOffspring")])]})]})})})});}
            var Q1;
            {var subQ2=makeQuery(id+"F3.opRevolve","SWEPT_FACE",FACE,{"disambiguationData":[OSD([sQuery(id+"F2.wireOp",EDGE,"E32")])]});var subQ4=makeQuery(id+"F1.opExtrude","SWEPT_FACE",FACE,{"disambiguationData":[OSD([sQuery(id+"F0.wireOp",EDGE,"E14.MirrorCS")])]});Q1=makeQuery(id+"F17.boolean.opBoolean","SPLIT",FACE,{"disambiguationData":[TD([subQ4])],"derivedFrom":makeQuery(id+"F7.boolean.opBoolean","SPLIT",FACE,{"disambiguationData":[TD([makeQuery(id+"F1.opExtrude","SWEPT_FACE",FACE,{"disambiguationData":[OSD([sQuery(id+"F0.wireOp",EDGE,"E9.MirrorCS")])]})])],"derivedFrom":makeQuery(id+"F5.boolean.opBoolean","SPLIT",FACE,{"disambiguationData":[TD([subQ2])],"derivedFrom":makeQuery(id+"F3.boolean.opBoolean","MERGE",FACE,{"derivedFrom":[makeQuery(id+"F1.opExtrude","SWEPT_FACE",FACE,{"disambiguationData":[OSD([sQuery(id+"F0.wireOp",EDGE,"E0")])]}),makeQuery(id+"F1.opExtrude","SWEPT_FACE",FACE,{"disambiguationData":[OSD([sQuery(id+"F0.wireOp",EDGE,"E17.trimOffspring")])]}),makeQuery(id+"F3.opRevolve","SWEPT_FACE",FACE,{"disambiguationData":[OSD([sQuery(id+"F2.wireOp",EDGE,"E31")])]}),makeQuery(id+"F3.opRevolve","SWEPT_FACE",FACE,{"disambiguationData":[OSD([sQuery(id+"F2.wireOp",EDGE,"E35")])]}),makeQuery(id+"F3.opRevolve","SWEPT_FACE",FACE,{"disambiguationData":[OSD([sQuery(id+"F2.wireOp",EDGE,"E51.trimOffspring")])]})]})})})});}
            var Q2;
            {var subQ1=sQuery(id+"F0.wireOp",EDGE,"E17.trimOffspring");var subQ3=makeQuery(id+"F3.opRevolve","SWEPT_FACE",FACE,{"disambiguationData":[OSD([sQuery(id+"F2.wireOp",EDGE,"E42")])]});var subQ4=sQuery(id+"F0.wireOp",EDGE,"E9.MirrorCS");var subQ5=sQuery(id+"F0.wireOp",EDGE,"E0");Q2=makeQuery(id+"F7.boolean.opBoolean","SPLIT",FACE,{"disambiguationData":[TD([makeQuery(id+"F1.opExtrude","SWEPT_FACE",FACE,{"disambiguationData":[OSD([subQ4])]})])],"derivedFrom":makeQuery(id+"F5.boolean.opBoolean","SPLIT",FACE,{"disambiguationData":[TD([subQ3])],"derivedFrom":makeQuery(id+"F3.boolean.opBoolean","MERGE",FACE,{"derivedFrom":[makeQuery(id+"F1.opExtrude","SWEPT_FACE",FACE,{"disambiguationData":[OSD([subQ5])]}),makeQuery(id+"F1.opExtrude","SWEPT_FACE",FACE,{"disambiguationData":[OSD([subQ1])]}),makeQuery(id+"F3.opRevolve","SWEPT_FACE",FACE,{"disambiguationData":[OSD([sQuery(id+"F2.wireOp",EDGE,"E31")])]}),makeQuery(id+"F3.opRevolve","SWEPT_FACE",FACE,{"disambiguationData":[OSD([sQuery(id+"F2.wireOp",EDGE,"E35")])]}),makeQuery(id+"F3.opRevolve","SWEPT_FACE",FACE,{"disambiguationData":[OSD([sQuery(id+"F2.wireOp",EDGE,"E51.trimOffspring")])]})]})})});}
            var Q3;
            {var subQ0=sQuery(id+"F0.wireOp",EDGE,"E17.trimOffspring");var subQ4=sQuery(id+"F0.wireOp",EDGE,"E9.MirrorCS");var subQ5=sQuery(id+"F0.wireOp",EDGE,"E0");var subQ7=makeQuery(id+"F3.opRevolve","SWEPT_FACE",FACE,{"disambiguationData":[OSD([sQuery(id+"F2.wireOp",EDGE,"E34")])]});Q3=makeQuery(id+"F7.boolean.opBoolean","SPLIT",FACE,{"disambiguationData":[TD([makeQuery(id+"F1.opExtrude","SWEPT_FACE",FACE,{"disambiguationData":[OSD([subQ4])]})])],"derivedFrom":makeQuery(id+"F5.boolean.opBoolean","SPLIT",FACE,{"disambiguationData":[TD([subQ7])],"derivedFrom":makeQuery(id+"F3.boolean.opBoolean","MERGE",FACE,{"derivedFrom":[makeQuery(id+"F1.opExtrude","SWEPT_FACE",FACE,{"disambiguationData":[OSD([subQ5])]}),makeQuery(id+"F1.opExtrude","SWEPT_FACE",FACE,{"disambiguationData":[OSD([subQ0])]}),makeQuery(id+"F3.opRevolve","SWEPT_FACE",FACE,{"disambiguationData":[OSD([sQuery(id+"F2.wireOp",EDGE,"E31")])]}),makeQuery(id+"F3.opRevolve","SWEPT_FACE",FACE,{"disambiguationData":[OSD([sQuery(id+"F2.wireOp",EDGE,"E35")])]}),makeQuery(id+"F3.opRevolve","SWEPT_FACE",FACE,{"disambiguationData":[OSD([sQuery(id+"F2.wireOp",EDGE,"E51.trimOffspring")])]})]})})});}
            var Q4;
            {var subQ0=sQuery(id+"F0.wireOp",EDGE,"E17.trimOffspring");var subQ2=sQuery(id+"F0.wireOp",EDGE,"E3");var subQ4=makeQuery(id+"F3.opRevolve","SWEPT_FACE",FACE,{"disambiguationData":[OSD([sQuery(id+"F2.wireOp",EDGE,"E42")])]});var subQ5=sQuery(id+"F0.wireOp",EDGE,"E0");Q4=makeQuery(id+"F7.boolean.opBoolean","SPLIT",FACE,{"disambiguationData":[TD([makeQuery(id+"F1.opExtrude","SWEPT_FACE",FACE,{"disambiguationData":[OSD([subQ2])]})])],"derivedFrom":makeQuery(id+"F5.boolean.opBoolean","SPLIT",FACE,{"disambiguationData":[TD([subQ4])],"derivedFrom":makeQuery(id+"F3.boolean.opBoolean","MERGE",FACE,{"derivedFrom":[makeQuery(id+"F1.opExtrude","SWEPT_FACE",FACE,{"disambiguationData":[OSD([subQ5])]}),makeQuery(id+"F1.opExtrude","SWEPT_FACE",FACE,{"disambiguationData":[OSD([subQ0])]}),makeQuery(id+"F3.opRevolve","SWEPT_FACE",FACE,{"disambiguationData":[OSD([sQuery(id+"F2.wireOp",EDGE,"E31")])]}),makeQuery(id+"F3.opRevolve","SWEPT_FACE",FACE,{"disambiguationData":[OSD([sQuery(id+"F2.wireOp",EDGE,"E35")])]}),makeQuery(id+"F3.opRevolve","SWEPT_FACE",FACE,{"disambiguationData":[OSD([sQuery(id+"F2.wireOp",EDGE,"E51.trimOffspring")])]})]})})});}
            var Q5;
            {var subQ2=makeQuery(id+"F3.opRevolve","SWEPT_FACE",FACE,{"disambiguationData":[OSD([sQuery(id+"F2.wireOp",EDGE,"E32")])]});var subQ4=makeQuery(id+"F1.opExtrude","SWEPT_FACE",FACE,{"disambiguationData":[OSD([sQuery(id+"F0.wireOp",EDGE,"E6.MirrorCS")])]});Q5=makeQuery(id+"F17.boolean.opBoolean","SPLIT",FACE,{"disambiguationData":[TD([subQ4])],"derivedFrom":makeQuery(id+"F7.boolean.opBoolean","SPLIT",FACE,{"disambiguationData":[TD([makeQuery(id+"F1.opExtrude","SWEPT_FACE",FACE,{"disambiguationData":[OSD([sQuery(id+"F0.wireOp",EDGE,"E3")])]})])],"derivedFrom":makeQuery(id+"F5.boolean.opBoolean","SPLIT",FACE,{"disambiguationData":[TD([subQ2])],"derivedFrom":makeQuery(id+"F3.boolean.opBoolean","MERGE",FACE,{"derivedFrom":[makeQuery(id+"F1.opExtrude","SWEPT_FACE",FACE,{"disambiguationData":[OSD([sQuery(id+"F0.wireOp",EDGE,"E0")])]}),makeQuery(id+"F1.opExtrude","SWEPT_FACE",FACE,{"disambiguationData":[OSD([sQuery(id+"F0.wireOp",EDGE,"E17.trimOffspring")])]}),makeQuery(id+"F3.opRevolve","SWEPT_FACE",FACE,{"disambiguationData":[OSD([sQuery(id+"F2.wireOp",EDGE,"E31")])]}),makeQuery(id+"F3.opRevolve","SWEPT_FACE",FACE,{"disambiguationData":[OSD([sQuery(id+"F2.wireOp",EDGE,"E35")])]}),makeQuery(id+"F3.opRevolve","SWEPT_FACE",FACE,{"disambiguationData":[OSD([sQuery(id+"F2.wireOp",EDGE,"E51.trimOffspring")])]})]})})})});}
            var Q6;
            {var subQ0=sQuery(id+"F0.wireOp",EDGE,"E17.trimOffspring");var subQ2=sQuery(id+"F0.wireOp",EDGE,"E3");var subQ5=makeQuery(id+"F3.opRevolve","SWEPT_FACE",FACE,{"disambiguationData":[OSD([sQuery(id+"F2.wireOp",EDGE,"E34")])]});var subQ6=sQuery(id+"F0.wireOp",EDGE,"E0");Q6=makeQuery(id+"F7.boolean.opBoolean","SPLIT",FACE,{"disambiguationData":[TD([makeQuery(id+"F1.opExtrude","SWEPT_FACE",FACE,{"disambiguationData":[OSD([subQ2])]})])],"derivedFrom":makeQuery(id+"F5.boolean.opBoolean","SPLIT",FACE,{"disambiguationData":[TD([subQ5])],"derivedFrom":makeQuery(id+"F3.boolean.opBoolean","MERGE",FACE,{"derivedFrom":[makeQuery(id+"F1.opExtrude","SWEPT_FACE",FACE,{"disambiguationData":[OSD([subQ6])]}),makeQuery(id+"F1.opExtrude","SWEPT_FACE",FACE,{"disambiguationData":[OSD([subQ0])]}),makeQuery(id+"F3.opRevolve","SWEPT_FACE",FACE,{"disambiguationData":[OSD([sQuery(id+"F2.wireOp",EDGE,"E31")])]}),makeQuery(id+"F3.opRevolve","SWEPT_FACE",FACE,{"disambiguationData":[OSD([sQuery(id+"F2.wireOp",EDGE,"E35")])]}),makeQuery(id+"F3.opRevolve","SWEPT_FACE",FACE,{"disambiguationData":[OSD([sQuery(id+"F2.wireOp",EDGE,"E51.trimOffspring")])]})]})})});}
            var Q7;
            {var subQ3=makeQuery(id+"F1.opExtrude","SWEPT_FACE",FACE,{"disambiguationData":[OSD([sQuery(id+"F0.wireOp",EDGE,"E9.MirrorCS")])]});var subQ4=makeQuery(id+"F3.opRevolve","SWEPT_FACE",FACE,{"disambiguationData":[OSD([sQuery(id+"F2.wireOp",EDGE,"E49.MirrorCS")])]});Q7=makeQuery(id+"F7.boolean.opBoolean","SPLIT",FACE,{"disambiguationData":[TD([subQ3])],"derivedFrom":makeQuery(id+"F5.boolean.opBoolean","MERGE",FACE,{"derivedFrom":[makeQuery(id+"F3.boolean.opBoolean","SPLIT",FACE,{"disambiguationData":[TD([makeQuery(id+"F1.opExtrude","SWEPT_FACE",FACE,{"disambiguationData":[OSD([sQuery(id+"F0.wireOp",EDGE,"E10.MirrorCS")])]})])],"derivedFrom":subQ4}),makeQuery(id+"F3.boolean.opBoolean","SPLIT",FACE,{"disambiguationData":[TD([makeQuery(id+"F1.opExtrude","SWEPT_FACE",FACE,{"disambiguationData":[OSD([sQuery(id+"F0.wireOp",EDGE,"E3")])]})])],"derivedFrom":subQ4}),makeQuery(id+"F3.boolean.opBoolean","SPLIT",FACE,{"disambiguationData":[TD([makeQuery(id+"F1.opExtrude","SWEPT_FACE",FACE,{"disambiguationData":[OSD([sQuery(id+"F0.wireOp",EDGE,"E5")])]})])],"derivedFrom":subQ4}),makeQuery(id+"F3.boolean.opBoolean","SPLIT",FACE,{"disambiguationData":[TD([makeQuery(id+"F1.opExtrude","SWEPT_FACE",FACE,{"disambiguationData":[OSD([sQuery(id+"F0.wireOp",EDGE,"E12.MirrorCS")])]})])],"derivedFrom":subQ4}),makeQuery(id+"F3.boolean.opBoolean","SPLIT",FACE,{"disambiguationData":[TD([makeQuery(id+"F1.opExtrude","SWEPT_FACE",FACE,{"disambiguationData":[OSD([sQuery(id+"F0.wireOp",EDGE,"E8.MirrorCS")])]})])],"derivedFrom":subQ4}),makeQuery(id+"F3.boolean.opBoolean","SPLIT",FACE,{"disambiguationData":[TD([makeQuery(id+"F1.opExtrude","SWEPT_FACE",FACE,{"disambiguationData":[OSD([sQuery(id+"F0.wireOp",EDGE,"E6.MirrorCS")])]})])],"derivedFrom":subQ4}),makeQuery(id+"F5.opRevolve","SWEPT_FACE",FACE,{"disambiguationData":[OSD([sQuery(id+"F4.wireOp",EDGE,"E56")])]})]})});}
            var Q8;
            {var subQ3=makeQuery(id+"F1.opExtrude","SWEPT_FACE",FACE,{"disambiguationData":[OSD([sQuery(id+"F0.wireOp",EDGE,"E9.MirrorCS")])]});var subQ4=makeQuery(id+"F3.opRevolve","SWEPT_FACE",FACE,{"disambiguationData":[OSD([sQuery(id+"F2.wireOp",EDGE,"E33")])]});Q8=makeQuery(id+"F7.boolean.opBoolean","SPLIT",FACE,{"disambiguationData":[TD([subQ3])],"derivedFrom":makeQuery(id+"F5.boolean.opBoolean","MERGE",FACE,{"derivedFrom":[makeQuery(id+"F3.boolean.opBoolean","SPLIT",FACE,{"disambiguationData":[TD([makeQuery(id+"F1.opExtrude","SWEPT_FACE",FACE,{"disambiguationData":[OSD([sQuery(id+"F0.wireOp",EDGE,"E10.MirrorCS")])]})])],"derivedFrom":subQ4}),makeQuery(id+"F3.boolean.opBoolean","SPLIT",FACE,{"disambiguationData":[TD([makeQuery(id+"F1.opExtrude","SWEPT_FACE",FACE,{"disambiguationData":[OSD([sQuery(id+"F0.wireOp",EDGE,"E3")])]})])],"derivedFrom":subQ4}),makeQuery(id+"F3.boolean.opBoolean","SPLIT",FACE,{"disambiguationData":[TD([makeQuery(id+"F1.opExtrude","SWEPT_FACE",FACE,{"disambiguationData":[OSD([sQuery(id+"F0.wireOp",EDGE,"E5")])]})])],"derivedFrom":subQ4}),makeQuery(id+"F3.boolean.opBoolean","SPLIT",FACE,{"disambiguationData":[TD([makeQuery(id+"F1.opExtrude","SWEPT_FACE",FACE,{"disambiguationData":[OSD([sQuery(id+"F0.wireOp",EDGE,"E12.MirrorCS")])]})])],"derivedFrom":subQ4}),makeQuery(id+"F3.boolean.opBoolean","SPLIT",FACE,{"disambiguationData":[TD([makeQuery(id+"F1.opExtrude","SWEPT_FACE",FACE,{"disambiguationData":[OSD([sQuery(id+"F0.wireOp",EDGE,"E8.MirrorCS")])]})])],"derivedFrom":subQ4}),makeQuery(id+"F3.boolean.opBoolean","SPLIT",FACE,{"disambiguationData":[TD([makeQuery(id+"F1.opExtrude","SWEPT_FACE",FACE,{"disambiguationData":[OSD([sQuery(id+"F0.wireOp",EDGE,"E6.MirrorCS")])]})])],"derivedFrom":subQ4}),makeQuery(id+"F5.opRevolve","SWEPT_FACE",FACE,{"disambiguationData":[OSD([sQuery(id+"F4.wireOp",EDGE,"E62.MirrorCS")])]})]})});}
            var Q9;
            Q9=makeQuery(id+"F17.boolean.opBoolean","COPY",EDGE,{"derivedFrom":makeQuery(id+"F17.opExtrude","CAP_EDGE",EDGE,{"disambiguationData":[OSD([sQuery(id+"F16.wireOp",EDGE,"E92.MirrorCS")])],"isStart":false})});
            var Q10;
            Q10=makeQuery(id+"F17.boolean.opBoolean","COPY",EDGE,{"derivedFrom":makeQuery(id+"F17.opExtrude","CAP_EDGE",EDGE,{"disambiguationData":[OSD([sQuery(id+"F16.wireOp",EDGE,"E92.MirrorCS")])],"isStart":true})});
            var Q11;
            {var subQ1=makeQuery(id+"F1.opExtrude","SWEPT_FACE",FACE,{"disambiguationData":[OSD([sQuery(id+"F0.wireOp",EDGE,"E6.MirrorCS")])]});var subQ3=makeQuery(id+"F1.opExtrude","SWEPT_FACE",FACE,{"disambiguationData":[OSD([sQuery(id+"F0.wireOp",EDGE,"E3")])]});var subQ4=makeQuery(id+"F3.opRevolve","SWEPT_FACE",FACE,{"disambiguationData":[OSD([sQuery(id+"F2.wireOp",EDGE,"E33")])]});Q11=makeQuery(id+"F7.boolean.opBoolean","SPLIT",FACE,{"disambiguationData":[TD([subQ3])],"derivedFrom":makeQuery(id+"F5.boolean.opBoolean","MERGE",FACE,{"derivedFrom":[makeQuery(id+"F3.boolean.opBoolean","SPLIT",FACE,{"disambiguationData":[TD([makeQuery(id+"F1.opExtrude","SWEPT_FACE",FACE,{"disambiguationData":[OSD([sQuery(id+"F0.wireOp",EDGE,"E10.MirrorCS")])]})])],"derivedFrom":subQ4}),makeQuery(id+"F3.boolean.opBoolean","SPLIT",FACE,{"disambiguationData":[TD([subQ3])],"derivedFrom":subQ4}),makeQuery(id+"F3.boolean.opBoolean","SPLIT",FACE,{"disambiguationData":[TD([makeQuery(id+"F1.opExtrude","SWEPT_FACE",FACE,{"disambiguationData":[OSD([sQuery(id+"F0.wireOp",EDGE,"E5")])]})])],"derivedFrom":subQ4}),makeQuery(id+"F3.boolean.opBoolean","SPLIT",FACE,{"disambiguationData":[TD([makeQuery(id+"F1.opExtrude","SWEPT_FACE",FACE,{"disambiguationData":[OSD([sQuery(id+"F0.wireOp",EDGE,"E12.MirrorCS")])]})])],"derivedFrom":subQ4}),makeQuery(id+"F3.boolean.opBoolean","SPLIT",FACE,{"disambiguationData":[TD([makeQuery(id+"F1.opExtrude","SWEPT_FACE",FACE,{"disambiguationData":[OSD([sQuery(id+"F0.wireOp",EDGE,"E8.MirrorCS")])]})])],"derivedFrom":subQ4}),makeQuery(id+"F3.boolean.opBoolean","SPLIT",FACE,{"disambiguationData":[TD([subQ1])],"derivedFrom":subQ4}),makeQuery(id+"F5.opRevolve","SWEPT_FACE",FACE,{"disambiguationData":[OSD([sQuery(id+"F4.wireOp",EDGE,"E62.MirrorCS")])]})]})});}
            var Q12;
            {var subQ2=makeQuery(id+"F1.opExtrude","SWEPT_FACE",FACE,{"disambiguationData":[OSD([sQuery(id+"F0.wireOp",EDGE,"E6.MirrorCS")])]});var subQ3=makeQuery(id+"F1.opExtrude","SWEPT_FACE",FACE,{"disambiguationData":[OSD([sQuery(id+"F0.wireOp",EDGE,"E3")])]});var subQ4=makeQuery(id+"F3.opRevolve","SWEPT_FACE",FACE,{"disambiguationData":[OSD([sQuery(id+"F2.wireOp",EDGE,"E49.MirrorCS")])]});Q12=makeQuery(id+"F7.boolean.opBoolean","SPLIT",FACE,{"disambiguationData":[TD([subQ3])],"derivedFrom":makeQuery(id+"F5.boolean.opBoolean","MERGE",FACE,{"derivedFrom":[makeQuery(id+"F3.boolean.opBoolean","SPLIT",FACE,{"disambiguationData":[TD([makeQuery(id+"F1.opExtrude","SWEPT_FACE",FACE,{"disambiguationData":[OSD([sQuery(id+"F0.wireOp",EDGE,"E10.MirrorCS")])]})])],"derivedFrom":subQ4}),makeQuery(id+"F3.boolean.opBoolean","SPLIT",FACE,{"disambiguationData":[TD([subQ3])],"derivedFrom":subQ4}),makeQuery(id+"F3.boolean.opBoolean","SPLIT",FACE,{"disambiguationData":[TD([makeQuery(id+"F1.opExtrude","SWEPT_FACE",FACE,{"disambiguationData":[OSD([sQuery(id+"F0.wireOp",EDGE,"E5")])]})])],"derivedFrom":subQ4}),makeQuery(id+"F3.boolean.opBoolean","SPLIT",FACE,{"disambiguationData":[TD([makeQuery(id+"F1.opExtrude","SWEPT_FACE",FACE,{"disambiguationData":[OSD([sQuery(id+"F0.wireOp",EDGE,"E12.MirrorCS")])]})])],"derivedFrom":subQ4}),makeQuery(id+"F3.boolean.opBoolean","SPLIT",FACE,{"disambiguationData":[TD([makeQuery(id+"F1.opExtrude","SWEPT_FACE",FACE,{"disambiguationData":[OSD([sQuery(id+"F0.wireOp",EDGE,"E8.MirrorCS")])]})])],"derivedFrom":subQ4}),makeQuery(id+"F3.boolean.opBoolean","SPLIT",FACE,{"disambiguationData":[TD([subQ2])],"derivedFrom":subQ4}),makeQuery(id+"F5.opRevolve","SWEPT_FACE",FACE,{"disambiguationData":[OSD([sQuery(id+"F4.wireOp",EDGE,"E56")])]})]})});}
            var Q13;
            {var subQ0=sQuery(id+"F16.wireOp",EDGE,"E88");Q13=makeQuery(id+"F17.boolean.opBoolean","COPY",EDGE,{"disambiguationData":[TD([makeQuery(id+"F3.opRevolve","SWEPT_FACE",FACE,{"disambiguationData":[OSD([sQuery(id+"F2.wireOp",EDGE,"E32")])]})])],"derivedFrom":makeQuery(id+"F17.opExtrude","SWEPT_EDGE",EDGE,{"disambiguationData":[OSD([sQuery(id+"F16.wireOp",EDGE,"E87"),subQ0])]})});}
            chamfer(context, id + "F23", {"entities" : qUnion([Q0, Q1, Q2, Q3, Q4, Q5, Q6, Q7, Q8, Q9, Q10, Q11, Q12, Q13]), "width" : 1.27 * mm, "tangentPropagation" : true});
        }
    });
